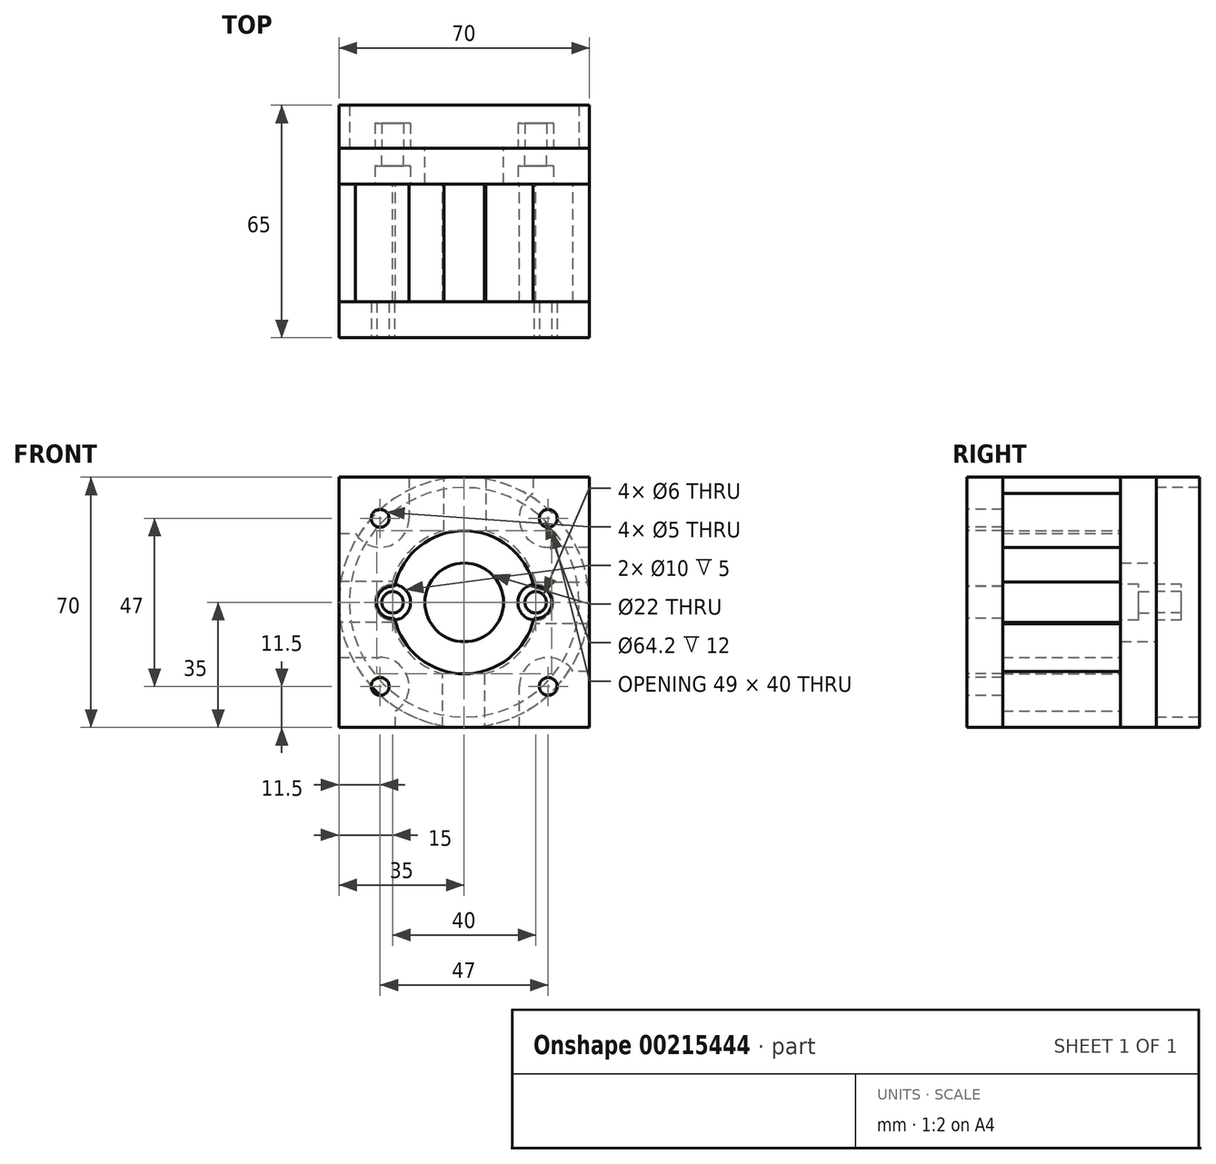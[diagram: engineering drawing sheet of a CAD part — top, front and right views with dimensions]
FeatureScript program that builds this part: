
annotation { "Feature Type Name" : "Feature", "Feature Type Description" : "" }
export const myFeature = defineFeature(function(context is Context, id is Id, definition is map)
    precondition{}
    {
        {
            var Q0;
            Q0=qCreatedBy(makeId("Front.planeOp"),FACE);
            var sketch = newSketch(context, id + "F0", { "sketchPlane" : qUnion([Q0])});
            skCircle(sketch, "E0", {"center": v(-20, 0) * mm, "radius": 5 * mm});
            skCircle(sketch, "E1", {"center": v(20, 0) * mm, "radius": 5 * mm});
            skCircle(sketch, "E2", {"center": v(-20, 0) * mm, "radius": 3 * mm});
            skCircle(sketch, "E3", {"center": v(20, 0) * mm, "radius": 3 * mm});
            skSolve(sketch);
        }
        {
            var Q0;
            Q0=makeQuery(id+"F0.imprint","IMPRINT",FACE,{"disambiguationData":[TD([[makeQuery(id+"F0.imprint","IMPRINT",EDGE,{"derivedFrom":sQuery(id+"F0.wireOp",EDGE,"E0")}),1.0]])]});
            var Q1;
            Q1=makeQuery(id+"F0.imprint","IMPRINT",FACE,{"disambiguationData":[TD([[makeQuery(id+"F0.imprint","IMPRINT",EDGE,{"derivedFrom":sQuery(id+"F0.wireOp",EDGE,"E1")}),1.0]])]});
            var Q2;
            Q2=sQuery(id+"F0.wireOp",EDGE,"E0");
            var Q3;
            Q3=sQuery(id+"F0.wireOp",EDGE,"E2");
            var Q4;
            Q4=sQuery(id+"F0.wireOp",EDGE,"E3");
            var Q5;
            Q5=sQuery(id+"F0.wireOp",EDGE,"E1");
            extrude(context, id + "F1", {"entities" : qUnion([Q0, Q1]), "surfaceEntities" : qUnion([Q2, Q3, Q4, Q5]), "oppositeDirection" : true, "depth" : 7 * mm});
        }
        {
            var Q0;
            Q0=qCreatedBy(makeId("Front.planeOp"),FACE);
            var sketch = newSketch(context, id + "F2", { "sketchPlane" : qUnion([Q0])});
            skCircle(sketch, "E4", {"center": v(0, 0) * mm, "radius": 35 * mm});
            skCircle(sketch, "E5", {"center": v(0, 0) * mm, "radius": 32.1 * mm});
            skSolve(sketch);
        }
        {
            var Q0;
            Q0=makeQuery(id+"F2.imprint","IMPRINT",FACE,{"disambiguationData":[TD([[makeQuery(id+"F2.imprint","IMPRINT",EDGE,{"derivedFrom":sQuery(id+"F2.wireOp",EDGE,"E4")}),1.0]])]});
            var Q1;
            Q1=sQuery(id+"F2.wireOp",EDGE,"E4");
            var Q2;
            Q2=sQuery(id+"F2.wireOp",EDGE,"E5");
            extrude(context, id + "F3", {"entities" : qUnion([Q0]), "surfaceEntities" : qUnion([Q1, Q2]), "oppositeDirection" : true, "depth" : 12 * mm});
        }
        {
            var Q0;
            Q0=qCreatedBy(makeId("Front.planeOp"),FACE);
            var sketch = newSketch(context, id + "F4", { "sketchPlane" : qUnion([Q0])});
            skLineSegment(sketch, "E6.bottom", {"start": v(-35, 35) * mm, "end": v(35, 35) * mm});
            skLineSegment(sketch, "E6.top", {"start": v(-35, -35) * mm, "end": v(35, -35) * mm});
            skLineSegment(sketch, "E6.left", {"start": v(-35, 35) * mm, "end": v(-35, -35) * mm});
            skLineSegment(sketch, "E6.right", {"start": v(35, 35) * mm, "end": v(35, -35) * mm});
            skCircle(sketch, "E7", {"center": v(0, 0) * mm, "radius": 11 * mm});
            skCircle(sketch, "E8", {"center": v(20, 0) * mm, "radius": 3 * mm});
            skCircle(sketch, "E9", {"center": v(-20, 0) * mm, "radius": 3 * mm});
            skSolve(sketch);
        }
        {
            var Q0;
            Q0 = qSketchRegion(id + "F4", true);
            extrude(context, id + "F5", {"entities" : qUnion([Q0]), "depth" : 10 * mm});
        }
        {
            var Q0;
            Q0=qCreatedBy(makeId("Front.planeOp"),FACE);
            cPlane(context, id + "F6", {"entities" : qUnion([Q0]), "cplaneType" : CPlaneType.OFFSET, "offset" : 10 * mm, "width" : 150 * mm, "height" : 150 * mm});
        }
        {
            var Q0;
            Q0=qCreatedBy(id+"F6.planeOp",FACE);
            var sketch = newSketch(context, id + "F7", { "sketchPlane" : qUnion([Q0])});
            skCircle(sketch, "E10", {"center": v(-20, 0) * mm, "radius": 5 * mm});
            skCircle(sketch, "E11", {"center": v(20, 0) * mm, "radius": 5 * mm});
            skSolve(sketch);
        }
        {
            var Q0;
            Q0 = qSketchRegion(id + "F7", true);
            extrude(context, id + "F8", {"entities" : qUnion([Q0]), "operationType" : NewBodyOperationType.REMOVE, "oppositeDirection" : true, "depth" : 5 * mm});
        }
        {
            var Q0;
            Q0=qCreatedBy(makeId("Front.planeOp"),FACE);
            cPlane(context, id + "F9", {"entities" : qUnion([Q0]), "cplaneType" : CPlaneType.OFFSET, "offset" : 53 * mm, "width" : 150 * mm, "height" : 150 * mm});
        }
        {
            var Q0;
            Q0=qCreatedBy(id+"F9.planeOp",FACE);
            var sketch = newSketch(context, id + "F10", { "sketchPlane" : qUnion([Q0])});
            skLineSegment(sketch, "E12.bottom", {"start": v(-35, 35) * mm, "end": v(35, 35) * mm});
            skLineSegment(sketch, "E12.top", {"start": v(-35, -35) * mm, "end": v(35, -35) * mm});
            skLineSegment(sketch, "E12.left", {"start": v(-35, 35) * mm, "end": v(-35, -35) * mm});
            skLineSegment(sketch, "E12.right", {"start": v(35, 35) * mm, "end": v(35, -35) * mm});
            skCircle(sketch, "E13", {"center": v(0, 0) * mm, "radius": 20 * mm});
            skCircle(sketch, "E14", {"center": v(-23.5, 23.5) * mm, "radius": 2.5 * mm});
            skCircle(sketch, "E15", {"center": v(23.5, 23.5) * mm, "radius": 2.5 * mm});
            skCircle(sketch, "E16", {"center": v(-23.5, -23.5) * mm, "radius": 2.5 * mm});
            skCircle(sketch, "E17", {"center": v(23.5, -23.5) * mm, "radius": 2.5 * mm});
            skCircle(sketch, "E18", {"center": v(-20, 0) * mm, "radius": 4.5 * mm});
            skCircle(sketch, "E19", {"center": v(20, 0) * mm, "radius": 4.5 * mm});
            skSolve(sketch);
        }
        {
            var Q0;
            Q0 = qSketchRegion(id + "F10", true);
            extrude(context, id + "F11", {"entities" : qUnion([Q0]), "oppositeDirection" : true, "depth" : 10 * mm});
        }
        {
            var Q0;
            Q0=qCreatedBy(id+"F6.planeOp",FACE);
            var sketch = newSketch(context, id + "F12", { "sketchPlane" : qUnion([Q0])});
            skLineSegment(sketch, "E20", {"start": v(-35, 6) * mm, "end": v(-20, 6) * mm});
            skArc(sketch, "E21", {"start": v(-15.4, 23.5) * mm, "mid": v(-21.3, 15.7) * mm, "end": v(-30.4, 19.28) * mm});
            skLineSegment(sketch, "E22", {"start": v(-35, 6) * mm, "end": v(-35, 19.28) * mm});
            skLineSegment(sketch, "E23", {"start": v(-35, 19.28) * mm, "end": v(-30.4, 19.28) * mm});
            skArc(sketch, "E24", {"start": v(-5.66, 20) * mm, "mid": v(-14.7, 14.93) * mm, "end": v(-20, 6) * mm});
            skPoint(sketch, "E25.center", {"position": v(0, 0) * mm});
            skLineSegment(sketch, "E26", {"start": v(-5.66, 20) * mm, "end": v(-5.66, 35) * mm});
            skLineSegment(sketch, "E27", {"start": v(-5.66, 35) * mm, "end": v(-15.4, 35) * mm});
            skLineSegment(sketch, "E28", {"start": v(-15.4, 35) * mm, "end": v(-15.4, 23.5) * mm});
            skLineSegment(sketch, "E29.1.0", {"start": v(-35, -5.66) * mm, "end": v(-35, -15.4) * mm});
            skLineSegment(sketch, "E29.1.1", {"start": v(-20, -5.66) * mm, "end": v(-35, -5.66) * mm});
            skArc(sketch, "E29.1.2", {"start": v(-20, -5.66) * mm, "mid": v(-14.93, -14.7) * mm, "end": v(-6, -20) * mm});
            skLineSegment(sketch, "E29.1.3", {"start": v(-6, -35) * mm, "end": v(-6, -20) * mm});
            skLineSegment(sketch, "E29.1.4", {"start": v(-6, -35) * mm, "end": v(-19.28, -35) * mm});
            skLineSegment(sketch, "E29.1.5", {"start": v(-19.28, -35) * mm, "end": v(-19.28, -30.4) * mm});
            skArc(sketch, "E29.1.6", {"start": v(-23.5, -15.4) * mm, "mid": v(-15.7, -21.3) * mm, "end": v(-19.28, -30.4) * mm});
            skLineSegment(sketch, "E29.1.7", {"start": v(-35, -15.4) * mm, "end": v(-23.5, -15.4) * mm});
            skLineSegment(sketch, "E29.2.0", {"start": v(5.66, -35) * mm, "end": v(15.4, -35) * mm});
            skLineSegment(sketch, "E29.2.1", {"start": v(5.66, -20) * mm, "end": v(5.66, -35) * mm});
            skArc(sketch, "E29.2.2", {"start": v(5.66, -20) * mm, "mid": v(14.7, -14.93) * mm, "end": v(20, -6) * mm});
            skLineSegment(sketch, "E29.2.3", {"start": v(35, -6) * mm, "end": v(20, -6) * mm});
            skLineSegment(sketch, "E29.2.4", {"start": v(35, -6) * mm, "end": v(35, -19.28) * mm});
            skLineSegment(sketch, "E29.2.5", {"start": v(35, -19.28) * mm, "end": v(30.4, -19.28) * mm});
            skArc(sketch, "E29.2.6", {"start": v(15.4, -23.5) * mm, "mid": v(21.3, -15.7) * mm, "end": v(30.4, -19.28) * mm});
            skLineSegment(sketch, "E29.2.7", {"start": v(15.4, -35) * mm, "end": v(15.4, -23.5) * mm});
            skLineSegment(sketch, "E29.3.0", {"start": v(35, 5.66) * mm, "end": v(35, 15.4) * mm});
            skLineSegment(sketch, "E29.3.1", {"start": v(20, 5.66) * mm, "end": v(35, 5.66) * mm});
            skArc(sketch, "E29.3.2", {"start": v(20, 5.66) * mm, "mid": v(14.93, 14.7) * mm, "end": v(6, 20) * mm});
            skLineSegment(sketch, "E29.3.3", {"start": v(6, 35) * mm, "end": v(6, 20) * mm});
            skLineSegment(sketch, "E29.3.4", {"start": v(6, 35) * mm, "end": v(19.28, 35) * mm});
            skLineSegment(sketch, "E29.3.5", {"start": v(19.28, 35) * mm, "end": v(19.28, 30.4) * mm});
            skArc(sketch, "E29.3.6", {"start": v(23.5, 15.4) * mm, "mid": v(15.7, 21.3) * mm, "end": v(19.28, 30.4) * mm});
            skLineSegment(sketch, "E29.3.7", {"start": v(35, 15.4) * mm, "end": v(23.5, 15.4) * mm});
            skSolve(sketch);
        }
        {
            var Q0;
            Q0 = qSketchRegion(id + "F12", true);
            extrude(context, id + "F13", {"entities" : qUnion([Q0]), "depth" : 33 * mm});
        }
    });
